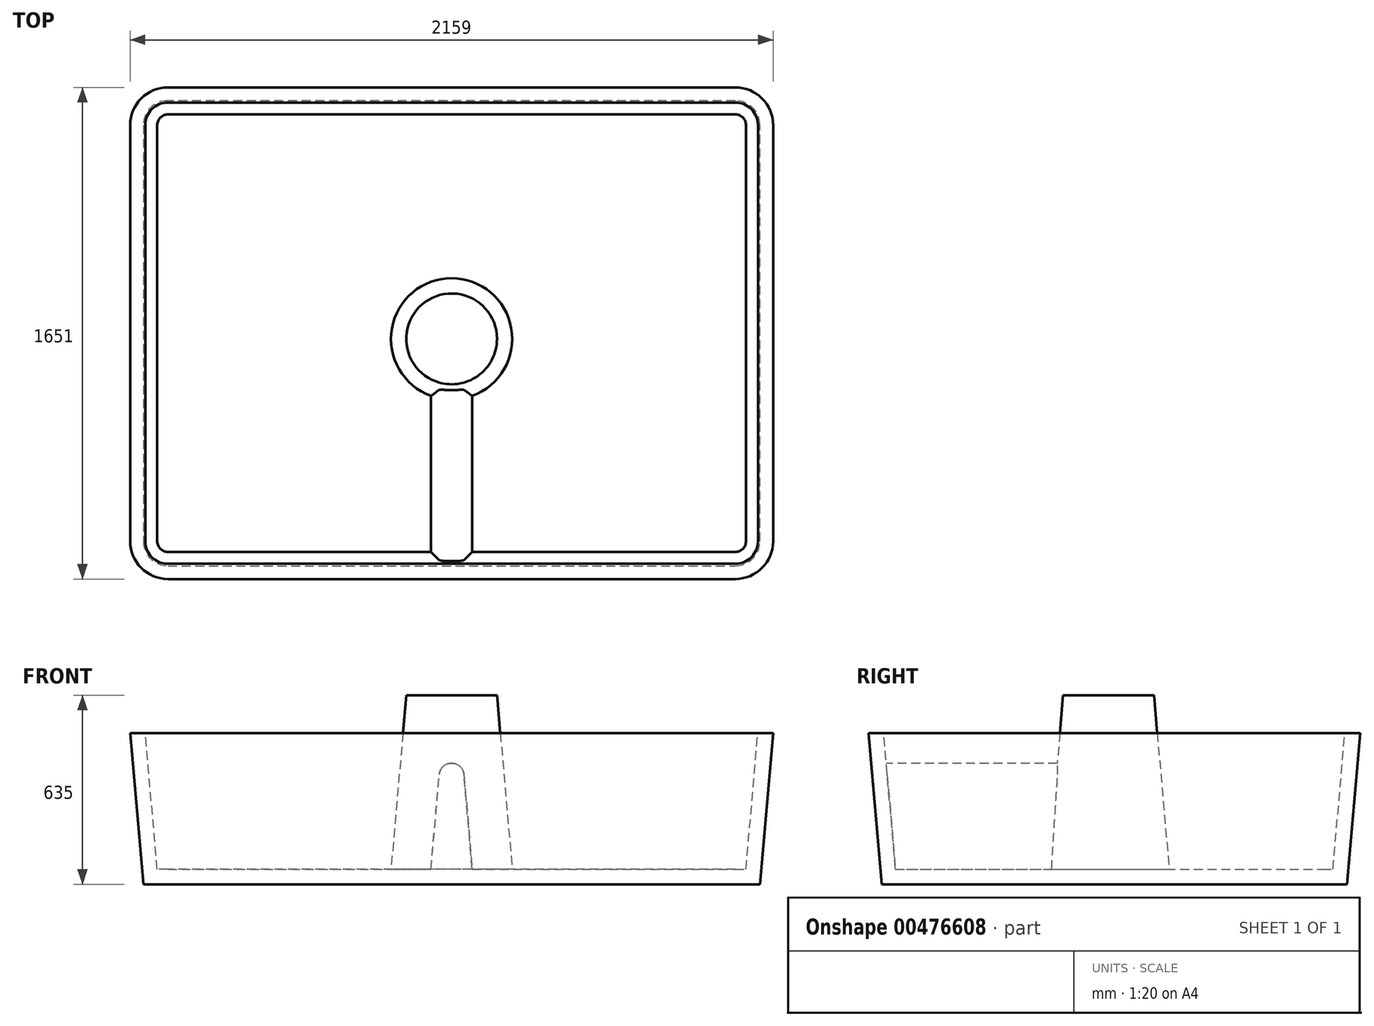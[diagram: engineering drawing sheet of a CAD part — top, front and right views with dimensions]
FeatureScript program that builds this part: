
annotation { "Feature Type Name" : "Feature", "Feature Type Description" : "" }
export const myFeature = defineFeature(function(context is Context, id is Id, definition is map)
    precondition{}
    {
        {
            var Q0;
            Q0=qCreatedBy(makeId("Top.planeOp"),FACE);
            var sketch = newSketch(context, id + "F0", { "sketchPlane" : qUnion([Q0])});
            skLineSegment(sketch, "E0.bottom", {"start": v(952.5, 825.5) * mm, "end": v(-952.5, 825.5) * mm});
            skLineSegment(sketch, "E0.top", {"start": v(952.5, -825.5) * mm, "end": v(-952.5, -825.5) * mm});
            skLineSegment(sketch, "E0.left", {"start": v(1079.5, 698.5) * mm, "end": v(1079.5, -698.5) * mm});
            skLineSegment(sketch, "E0.right", {"start": v(-1079.5, 698.5) * mm, "end": v(-1079.5, -698.5) * mm});
            skPoint(sketch, "E0.middle", {"position": v(0, 0) * mm});
            skPoint(sketch, "E1.visualSharp", {"position": v(-1079.5, 825.5) * mm});
            skArc(sketch, "E1.filletArc", {"start": v(-952.5, 825.5) * mm, "mid": v(-1042.3, 788.3) * mm, "end": v(-1079.5, 698.5) * mm});
            skPoint(sketch, "E2.visualSharp", {"position": v(1079.5, 825.5) * mm});
            skArc(sketch, "E2.filletArc", {"start": v(1079.5, 698.5) * mm, "mid": v(1042.3, 788.3) * mm, "end": v(952.5, 825.5) * mm});
            skPoint(sketch, "E3.visualSharp", {"position": v(-1079.5, -825.5) * mm});
            skArc(sketch, "E3.filletArc", {"start": v(-1079.5, -698.5) * mm, "mid": v(-1042.3, -788.3) * mm, "end": v(-952.5, -825.5) * mm});
            skPoint(sketch, "E4.visualSharp", {"position": v(1079.5, -825.5) * mm});
            skArc(sketch, "E4.filletArc", {"start": v(952.5, -825.5) * mm, "mid": v(1042.3, -788.3) * mm, "end": v(1079.5, -698.5) * mm});
            skSolve(sketch);
        }
        {
            var Q0;
            Q0 = qSketchRegion(id + "F0", true);
            extrude(context, id + "F1", {"entities" : qUnion([Q0]), "oppositeDirection" : true, "depth" : 508 * mm, "hasDraft" : true, "draftAngle" : 5 * degree, "draftPullDirection" : true});
        }
        {
            var Q0;
            Q0=makeQuery(id+"F1.opExtrude","CAP_FACE",FACE,{"disambiguationData":[OSD([sQuery(id+"F0.wireOp",EDGE,"E0.bottom"),sQuery(id+"F0.wireOp",EDGE,"E0.top"),sQuery(id+"F0.wireOp",EDGE,"E0.left"),sQuery(id+"F0.wireOp",EDGE,"E0.right"),sQuery(id+"F0.wireOp",EDGE,"E1.filletArc"),sQuery(id+"F0.wireOp",EDGE,"E2.filletArc"),sQuery(id+"F0.wireOp",EDGE,"E3.filletArc"),sQuery(id+"F0.wireOp",EDGE,"E4.filletArc")])],"isStart":true});
            shell(context, id + "F2", {"entities" : qUnion([Q0]), "thickness" : 50.8 * mm});
        }
        {
            var Q0;
            Q0=qCreatedBy(makeId("Top.planeOp"),FACE);
            cPlane(context, id + "F3", {"entities" : qUnion([Q0]), "cplaneType" : CPlaneType.OFFSET, "offset" : 127 * mm, "width" : 152.4 * mm, "height" : 152.4 * mm});
        }
        {
            var Q0;
            Q0=qCreatedBy(id+"F3.planeOp",FACE);
            var sketch = newSketch(context, id + "F4", { "sketchPlane" : qUnion([Q0])});
            skCircle(sketch, "E5", {"center": v(0, -19.14) * mm, "radius": 152.4 * mm});
            skSolve(sketch);
        }
        {
            var Q0;
            Q0 = qSketchRegion(id + "F4", true);
            extrude(context, id + "F5", {"entities" : qUnion([Q0]), "operationType" : NewBodyOperationType.ADD, "oppositeDirection" : true, "depth" : 584.2 * mm, "hasDraft" : true, "draftAngle" : 5 * degree});
        }
        {
            var Q0;
            Q0=qCreatedBy(makeId("Top.planeOp"),FACE);
            cPlane(context, id + "F6", {"entities" : qUnion([Q0]), "cplaneType" : CPlaneType.OFFSET, "offset" : 101.6 * mm, "oppositeDirection" : true, "width" : 152.4 * mm, "height" : 152.4 * mm});
        }
        {
            var Q0;
            Q0=qCreatedBy(id+"F6.planeOp",FACE);
            var sketch = newSketch(context, id + "F7", { "sketchPlane" : qUnion([Q0])});
            skLineSegment(sketch, "E6.0", {"start": v(-38.1, 0) * mm, "end": v(-38.1, -770.34) * mm});
            skLineSegment(sketch, "E7.0", {"start": v(38.1, 0) * mm, "end": v(38.1, -770.34) * mm});
            skLineSegment(sketch, "E8", {"start": v(-38.1, 0) * mm, "end": v(38.1, 0) * mm});
            skLineSegment(sketch, "E9", {"start": v(-38.1, -770.34) * mm, "end": v(38.1, -770.34) * mm});
            skSolve(sketch);
        }
        {
            var Q0;
            Q0 = qSketchRegion(id + "F7", true);
            var Q1;
            Q1=makeQuery(id+"F2.opShell","OFFSET_FACE",FACE,{"disambiguationData":[OSD([sQuery(id+"F0.wireOp",EDGE,"E0.bottom"),sQuery(id+"F0.wireOp",EDGE,"E0.top"),sQuery(id+"F0.wireOp",EDGE,"E0.left"),sQuery(id+"F0.wireOp",EDGE,"E0.right"),sQuery(id+"F0.wireOp",EDGE,"E1.filletArc"),sQuery(id+"F0.wireOp",EDGE,"E2.filletArc"),sQuery(id+"F0.wireOp",EDGE,"E3.filletArc"),sQuery(id+"F0.wireOp",EDGE,"E4.filletArc")])]});
            extrude(context, id + "F8", {"entities" : qUnion([Q0, Q1]), "operationType" : NewBodyOperationType.ADD, "endBound" : BoundingType.UP_TO_NEXT, "oppositeDirection" : true, "depth" : 25.4 * mm, "hasDraft" : true, "draftAngle" : 5 * degree});
        }
        {
            var Q0;
            Q0=makeQuery(id+"F8.opExtrude","CAP_EDGE",EDGE,{"disambiguationData":[OSD([sQuery(id+"F7.wireOp",EDGE,"E7.0")])],"isStart":true});
            var Q1;
            Q1=makeQuery(id+"F8.opExtrude","CAP_EDGE",EDGE,{"disambiguationData":[OSD([sQuery(id+"F7.wireOp",EDGE,"E6.0")])],"isStart":true});
            fillet(context, id + "F9", {"entities" : qUnion([Q0, Q1]), "radius" : 41.27 * mm, "allowEdgeOverflow" : false});
        }
    });
